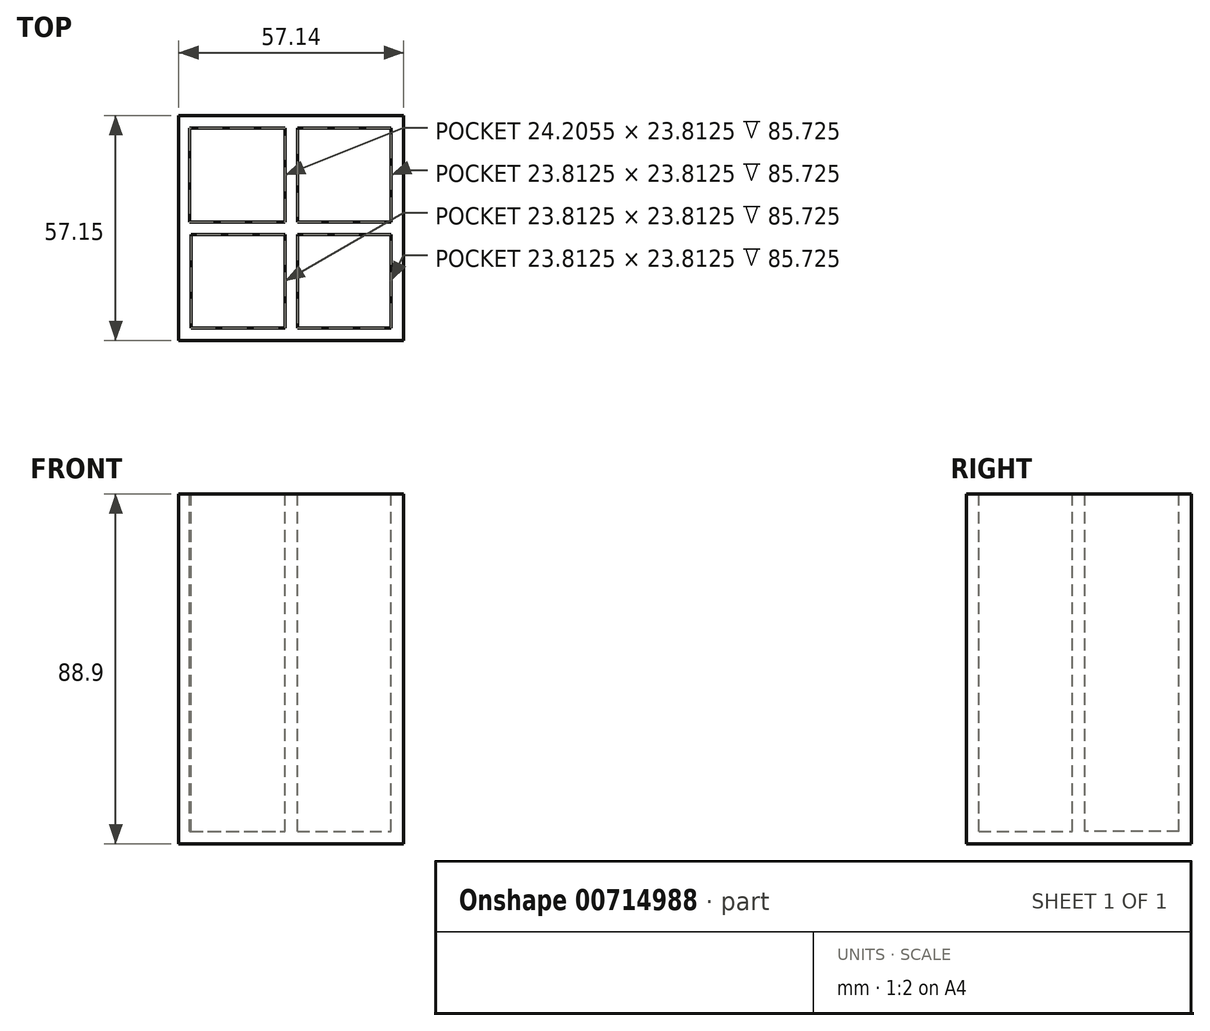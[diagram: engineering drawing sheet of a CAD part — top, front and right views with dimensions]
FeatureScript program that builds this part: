
annotation { "Feature Type Name" : "Feature", "Feature Type Description" : "" }
export const myFeature = defineFeature(function(context is Context, id is Id, definition is map)
    precondition{}
    {
        {
            var Q0;
            Q0=qCreatedBy(makeId("Front.planeOp"),FACE);
            var sketch = newSketch(context, id + "F0", { "sketchPlane" : qUnion([Q0])});
            skLineSegment(sketch, "E0.bottom", {"start": v(-28.57, 44.45) * mm, "end": v(28.58, 44.45) * mm});
            skLineSegment(sketch, "E0.top", {"start": v(-28.58, -44.45) * mm, "end": v(28.58, -44.45) * mm});
            skLineSegment(sketch, "E0.left", {"start": v(-28.57, 44.45) * mm, "end": v(-28.58, -44.45) * mm});
            skLineSegment(sketch, "E0.right", {"start": v(28.58, 44.45) * mm, "end": v(28.58, -44.45) * mm});
            skPoint(sketch, "E0.middle", {"position": v(0, 0) * mm});
            skSolve(sketch);
        }
        {
            var Q0;
            Q0=qSketchRegion(id+"F0",true);
            extrude(context, id + "F1", {"entities" : qUnion([Q0]), "depth" : 57.15 * mm, "offsetDistance" : 25.4 * mm});
        }
        {
            var Q0;
            Q0=makeQuery(id+"F1.opExtrude","SWEPT_FACE",FACE,{"disambiguationData":[OSD([sQuery(id+"F0.wireOp",EDGE,"E0.bottom")])]});
            var sketch = newSketch(context, id + "F2", { "sketchPlane" : qUnion([Q0])});
            skLineSegment(sketch, "E1.bottom", {"start": v(-25.8, -3.18) * mm, "end": v(-1.59, -3.18) * mm});
            skLineSegment(sketch, "E1.top", {"start": v(-25.8, -26.99) * mm, "end": v(-1.59, -26.99) * mm});
            skLineSegment(sketch, "E1.left", {"start": v(-25.8, -3.18) * mm, "end": v(-25.8, -26.99) * mm});
            skLineSegment(sketch, "E1.right", {"start": v(-1.59, -3.17) * mm, "end": v(-1.59, -26.99) * mm});
            skSolve(sketch);
        }
        {
            var Q0;
            Q0=qSketchRegion(id+"F2",true);
            extrude(context, id + "F3", {"entities" : qUnion([Q0]), "operationType" : NewBodyOperationType.REMOVE, "oppositeDirection" : true, "depth" : 85.72 * mm});
        }
        {
            var Q0;
            Q0=makeQuery(id+"F1.opExtrude","SWEPT_FACE",FACE,{"disambiguationData":[OSD([sQuery(id+"F0.wireOp",EDGE,"E0.bottom")])]});
            var sketch = newSketch(context, id + "F4", { "sketchPlane" : qUnion([Q0])});
            skLineSegment(sketch, "E2.bottom", {"start": v(-25.8, -3.18) * mm, "end": v(-1.59, -3.18) * mm});
            skLineSegment(sketch, "E2.top", {"start": v(-25.8, -26.99) * mm, "end": v(-1.59, -26.99) * mm});
            skLineSegment(sketch, "E2.left", {"start": v(-25.8, -3.18) * mm, "end": v(-25.8, -26.99) * mm});
            skLineSegment(sketch, "E2.right", {"start": v(-1.59, -3.18) * mm, "end": v(-1.59, -26.99) * mm});
            skLineSegment(sketch, "E3.bottom", {"start": v(1.59, -3.18) * mm, "end": v(25.4, -3.18) * mm});
            skLineSegment(sketch, "E3.top", {"start": v(1.59, -26.99) * mm, "end": v(25.4, -26.99) * mm});
            skLineSegment(sketch, "E3.left", {"start": v(1.59, -3.18) * mm, "end": v(1.59, -26.99) * mm});
            skLineSegment(sketch, "E3.right", {"start": v(25.4, -3.17) * mm, "end": v(25.4, -26.99) * mm});
            skSolve(sketch);
        }
        {
            var Q0;
            Q0=makeQuery(id+"F4.imprint","IMPRINT",FACE,{"disambiguationData":[TD([[makeQuery(id+"F4.imprint","IMPRINT",EDGE,{"derivedFrom":sQuery(id+"F4.wireOp",EDGE,"E3.bottom")}),-1.0]])]});
            extrude(context, id + "F5", {"entities" : qUnion([Q0]), "operationType" : NewBodyOperationType.REMOVE, "oppositeDirection" : true, "depth" : 85.72 * mm});
        }
        {
            var Q0;
            Q0=makeQuery(id+"F1.opExtrude","SWEPT_FACE",FACE,{"disambiguationData":[OSD([sQuery(id+"F0.wireOp",EDGE,"E0.bottom")])]});
            var sketch = newSketch(context, id + "F6", { "sketchPlane" : qUnion([Q0])});
            skLineSegment(sketch, "E4.bottom", {"start": v(-25.4, -53.98) * mm, "end": v(-1.59, -53.98) * mm});
            skLineSegment(sketch, "E4.top", {"start": v(-25.4, -30.16) * mm, "end": v(-1.59, -30.16) * mm});
            skLineSegment(sketch, "E4.left", {"start": v(-25.4, -53.98) * mm, "end": v(-25.4, -30.16) * mm});
            skLineSegment(sketch, "E4.right", {"start": v(-1.59, -53.98) * mm, "end": v(-1.59, -30.16) * mm});
            skSolve(sketch);
        }
        {
            var Q0;
            Q0=qSketchRegion(id+"F6",true);
            extrude(context, id + "F7", {"entities" : qUnion([Q0]), "operationType" : NewBodyOperationType.REMOVE, "oppositeDirection" : true, "depth" : 85.72 * mm});
        }
        {
            var Q0;
            Q0=makeQuery(id+"F1.opExtrude","SWEPT_FACE",FACE,{"disambiguationData":[OSD([sQuery(id+"F0.wireOp",EDGE,"E0.bottom")])]});
            var sketch = newSketch(context, id + "F8", { "sketchPlane" : qUnion([Q0])});
            skLineSegment(sketch, "E5.bottom", {"start": v(1.59, -30.16) * mm, "end": v(25.4, -30.16) * mm});
            skLineSegment(sketch, "E5.top", {"start": v(1.59, -53.98) * mm, "end": v(25.4, -53.98) * mm});
            skLineSegment(sketch, "E5.left", {"start": v(1.59, -30.16) * mm, "end": v(1.59, -53.98) * mm});
            skLineSegment(sketch, "E5.right", {"start": v(25.4, -30.16) * mm, "end": v(25.4, -53.98) * mm});
            skSolve(sketch);
        }
        {
            var Q0;
            Q0=qSketchRegion(id+"F8",true);
            extrude(context, id + "F9", {"entities" : qUnion([Q0]), "operationType" : NewBodyOperationType.REMOVE, "oppositeDirection" : true, "depth" : 85.72 * mm});
        }
    });
